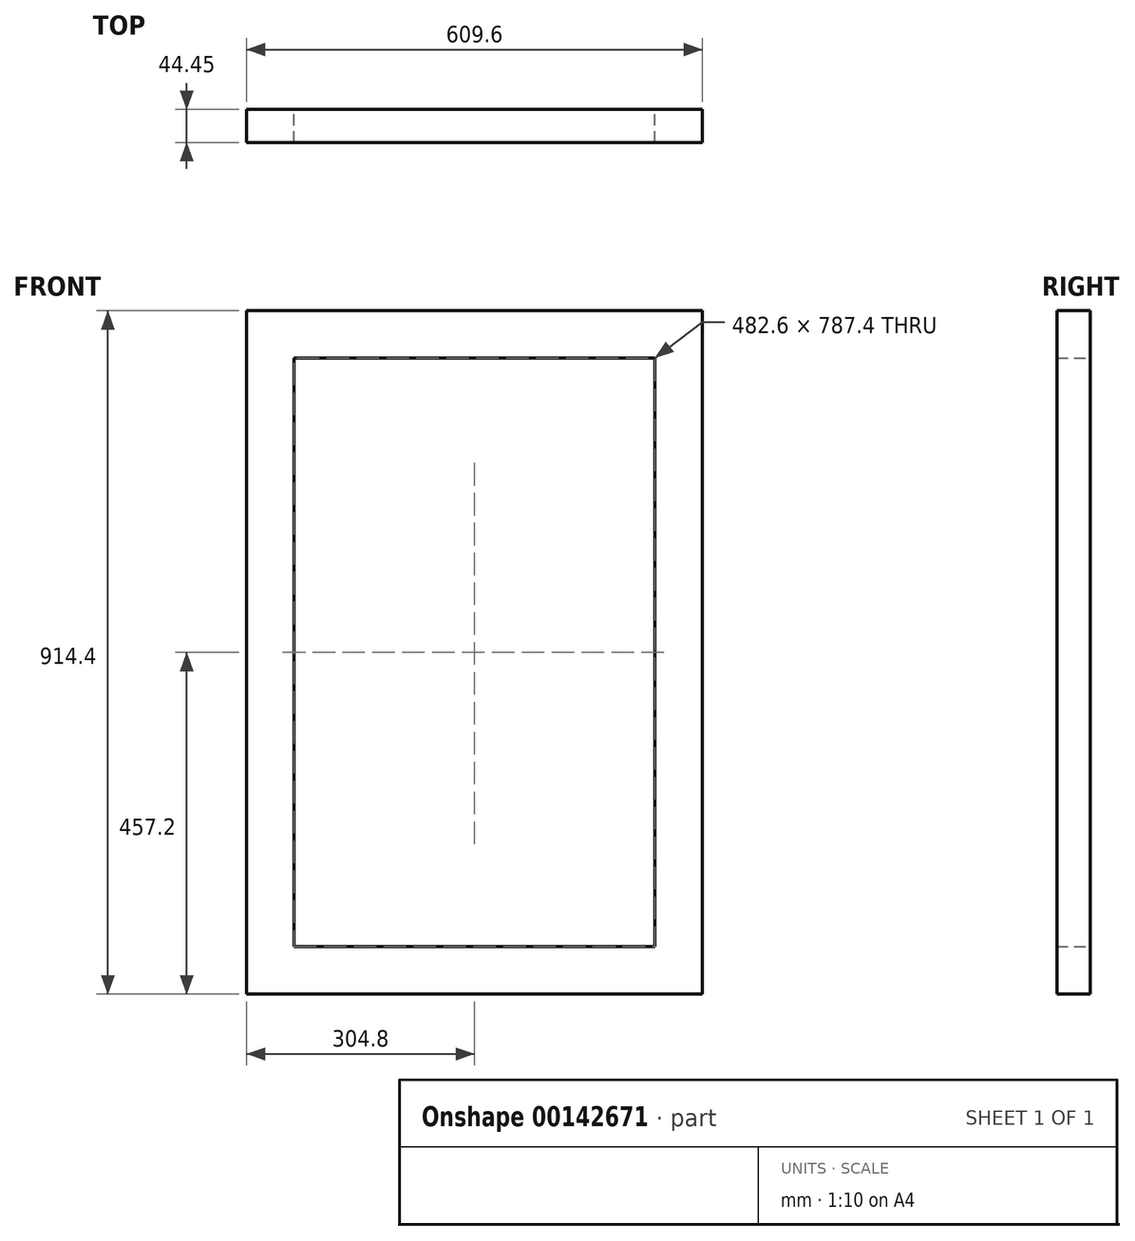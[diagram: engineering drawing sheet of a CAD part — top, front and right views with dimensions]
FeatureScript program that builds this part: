
annotation { "Feature Type Name" : "Feature", "Feature Type Description" : "" }
export const myFeature = defineFeature(function(context is Context, id is Id, definition is map)
    precondition{}
    {
        {
            var Q0;
            Q0=qCreatedBy(makeId("Front.planeOp"),FACE);
            var sketch = newSketch(context, id + "F0", { "sketchPlane" : qUnion([Q0])});
            skLineSegment(sketch, "E0.bottom", {"start": v(304.8, 457.2) * mm, "end": v(-304.8, 457.2) * mm});
            skLineSegment(sketch, "E0.top", {"start": v(304.8, -457.2) * mm, "end": v(-304.8, -457.2) * mm});
            skLineSegment(sketch, "E0.left", {"start": v(304.8, 457.2) * mm, "end": v(304.8, -457.2) * mm});
            skLineSegment(sketch, "E0.right", {"start": v(-304.8, 457.2) * mm, "end": v(-304.8, -457.2) * mm});
            skPoint(sketch, "E0.middle", {"position": v(0, 0) * mm});
            skLineSegment(sketch, "E1.bottom", {"start": v(241.3, 393.7) * mm, "end": v(-241.3, 393.7) * mm});
            skLineSegment(sketch, "E1.top", {"start": v(241.3, -393.7) * mm, "end": v(-241.3, -393.7) * mm});
            skLineSegment(sketch, "E1.left", {"start": v(241.3, 393.7) * mm, "end": v(241.3, -393.7) * mm});
            skLineSegment(sketch, "E1.right", {"start": v(-241.3, 393.7) * mm, "end": v(-241.3, -393.7) * mm});
            skSolve(sketch);
        }
        {
            var Q0;
            Q0 = qSketchRegion(id + "F0", true);
            extrude(context, id + "F1", {"entities" : qUnion([Q0]), "depth" : 44.45 * mm});
        }
    });
